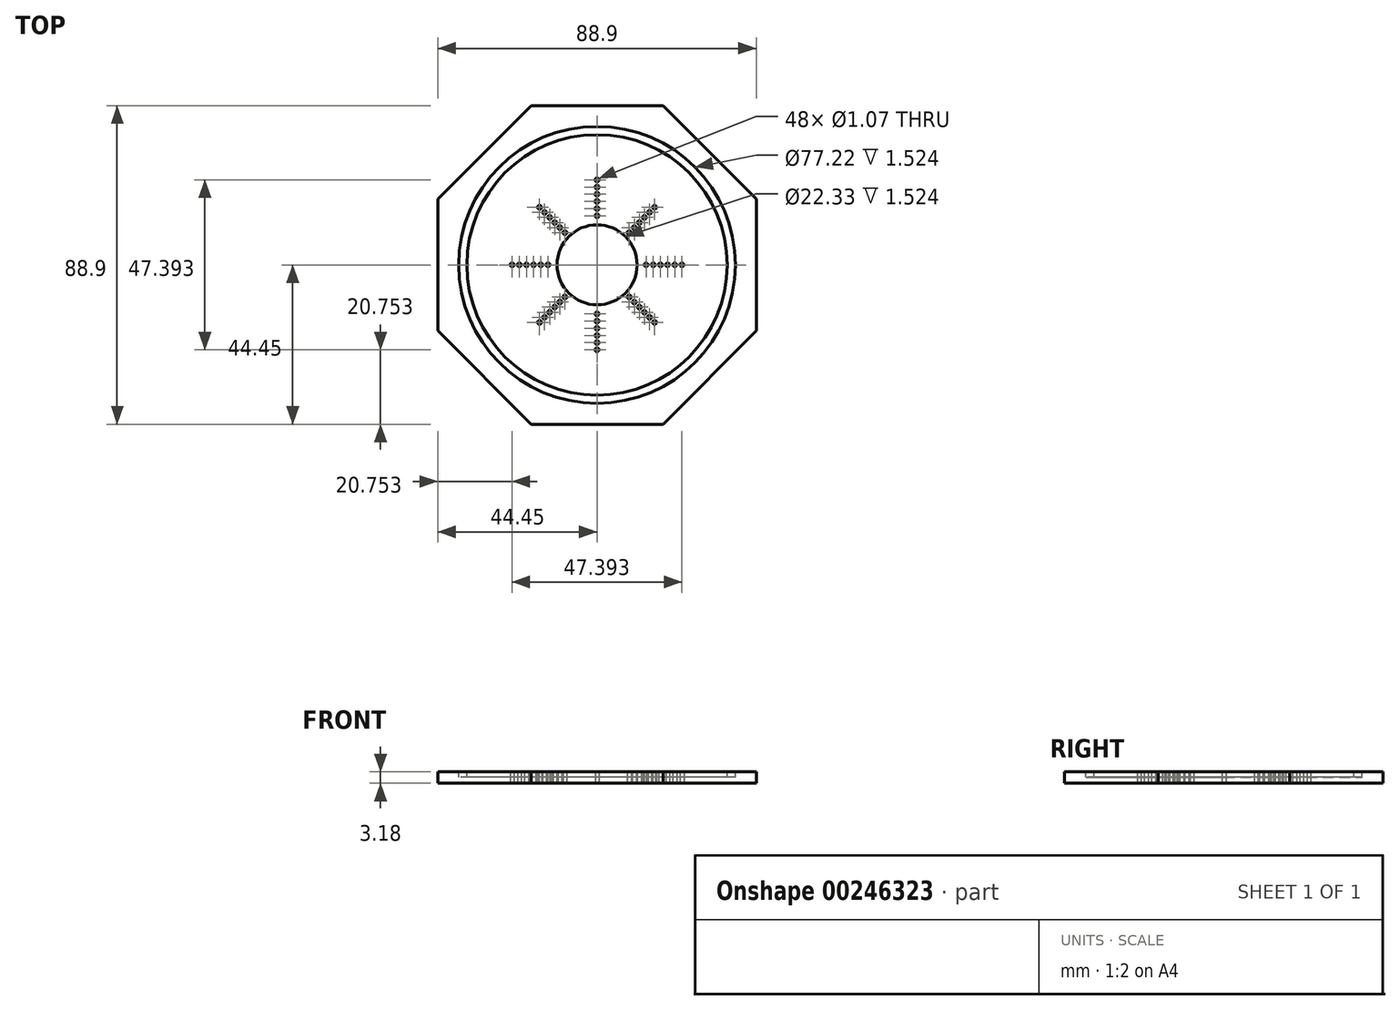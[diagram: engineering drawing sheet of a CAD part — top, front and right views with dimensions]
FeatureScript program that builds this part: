
annotation { "Feature Type Name" : "Feature", "Feature Type Description" : "" }
export const myFeature = defineFeature(function(context is Context, id is Id, definition is map)
    precondition{}
    {
        {
            var Q0;
            Q0=qCreatedBy(makeId("Top.planeOp"),FACE);
            var sketch = newSketch(context, id + "F0", { "sketchPlane" : qUnion([Q0])});
            skCircle(sketch, "E0", {"center": v(0, 0) * mm, "radius": 44.45 * mm, "construction": true});
            skLineSegment(sketch, "E1.bottom", {"start": v(-18.41, 44.45) * mm, "end": v(18.41, 44.45) * mm});
            skLineSegment(sketch, "E1.top", {"start": v(-18.41, -44.45) * mm, "end": v(18.41, -44.45) * mm});
            skLineSegment(sketch, "E1.left", {"start": v(-44.45, 18.41) * mm, "end": v(-44.45, -18.41) * mm});
            skLineSegment(sketch, "E1.right", {"start": v(44.45, 18.41) * mm, "end": v(44.45, -18.41) * mm});
            skLineSegment(sketch, "E2", {"start": v(-44.45, 18.41) * mm, "end": v(-18.41, 44.45) * mm});
            skLineSegment(sketch, "E3", {"start": v(0, 44.45) * mm, "end": v(0, -44.45) * mm, "construction": true});
            skLineSegment(sketch, "E4.MirrorCS", {"start": v(44.45, 18.41) * mm, "end": v(18.41, 44.45) * mm});
            skLineSegment(sketch, "E5", {"start": v(-44.45, 0) * mm, "end": v(44.45, 0) * mm});
            skLineSegment(sketch, "E6.MirrorCS", {"start": v(-44.45, -18.41) * mm, "end": v(-18.41, -44.45) * mm});
            skLineSegment(sketch, "E7.MirrorCS", {"start": v(44.45, -18.41) * mm, "end": v(18.41, -44.45) * mm});
            skPoint(sketch, "E8.orphan", {"position": v(-44.45, 44.45) * mm});
            skPoint(sketch, "E9.orphan", {"position": v(44.45, 44.45) * mm});
            skPoint(sketch, "E10.orphan", {"position": v(44.45, -44.45) * mm});
            skPoint(sketch, "E11.orphan", {"position": v(-44.45, -44.45) * mm});
            skSolve(sketch);
        }
        {
            var Q0;
            Q0=qSketchRegion(id+"F0",true);
            extrude(context, id + "F1", {"entities" : qUnion([Q0]), "depth" : 3.17 * mm});
        }
        {
            var Q0;
            Q0=makeQuery(id+"F1.opExtrude","CAP_FACE",FACE,{"disambiguationData":[OSD([sQuery(id+"F0.wireOp",EDGE,"E1.bottom"),sQuery(id+"F0.wireOp",EDGE,"E1.top"),sQuery(id+"F0.wireOp",EDGE,"E1.left"),sQuery(id+"F0.wireOp",EDGE,"E1.right")])],"isStart":false});
            var sketch = newSketch(context, id + "F2", { "sketchPlane" : qUnion([Q0])});
            skCircle(sketch, "E12", {"center": v(0, 0) * mm, "radius": 38.6 * mm});
            skCircle(sketch, "E13", {"center": v(0, 0) * mm, "radius": 36.32 * mm});
            skCircle(sketch, "E14", {"center": v(0, 0) * mm, "radius": 11.16 * mm});
            skSolve(sketch);
        }
        {
            var Q0;
            Q0=qSketchRegion(id+"F2",true);
            var Q1;
            Q1=makeQuery(id+"F2.imprint","IMPRINT",FACE,{"disambiguationData":[TD([[makeQuery(id+"F2.imprint","IMPRINT",EDGE,{"derivedFrom":sQuery(id+"F2.wireOp",EDGE,"E14")}),1.0]])]});
            extrude(context, id + "F3", {"entities" : qUnion([Q0, Q1]), "operationType" : NewBodyOperationType.REMOVE, "oppositeDirection" : true, "depth" : 1.52 * mm});
        }
        {
            var Q0;
            Q0=qCreatedBy(makeId("Top.planeOp"),FACE);
            var sketch = newSketch(context, id + "F4", { "sketchPlane" : qUnion([Q0])});
            skCircle(sketch, "E15", {"center": v(0, -13.7) * mm, "radius": 0.53 * mm});
            skCircle(sketch, "E16", {"center": v(0, -15.7) * mm, "radius": 0.53 * mm});
            skCircle(sketch, "E17", {"center": v(0, -17.7) * mm, "radius": 0.53 * mm});
            skCircle(sketch, "E18", {"center": v(0, -19.7) * mm, "radius": 0.53 * mm});
            skCircle(sketch, "E19", {"center": v(0, -21.7) * mm, "radius": 0.53 * mm});
            skCircle(sketch, "E20", {"center": v(0, -23.7) * mm, "radius": 0.53 * mm});
            skCircle(sketch, "E21.0", {"center": v(0, 0) * mm, "radius": 44.45 * mm, "construction": true});
            skLineSegment(sketch, "E22", {"start": v(31.43, 31.43) * mm, "end": v(-31.43, -31.43) * mm, "construction": true});
            skCircle(sketch, "E23", {"center": v(-8.98, -8.98) * mm, "radius": 0.53 * mm});
            skCircle(sketch, "E24", {"center": v(-10.4, -10.4) * mm, "radius": 0.53 * mm});
            skCircle(sketch, "E25", {"center": v(-11.8, -11.8) * mm, "radius": 0.53 * mm});
            skCircle(sketch, "E26", {"center": v(-13.22, -13.22) * mm, "radius": 0.53 * mm});
            skCircle(sketch, "E27", {"center": v(-14.63, -14.63) * mm, "radius": 0.53 * mm});
            skCircle(sketch, "E28", {"center": v(-16.05, -16.05) * mm, "radius": 0.53 * mm});
            skCircle(sketch, "E29.1.0", {"center": v(-21.7, 0) * mm, "radius": 0.53 * mm});
            skCircle(sketch, "E29.1.1", {"center": v(-23.7, 0) * mm, "radius": 0.53 * mm});
            skCircle(sketch, "E29.1.2", {"center": v(-13.7, 0) * mm, "radius": 0.53 * mm});
            skCircle(sketch, "E29.1.3", {"center": v(-17.7, 0) * mm, "radius": 0.53 * mm});
            skCircle(sketch, "E29.1.4", {"center": v(-15.7, 0) * mm, "radius": 0.53 * mm});
            skCircle(sketch, "E29.1.5", {"center": v(-19.7, 0) * mm, "radius": 0.53 * mm});
            skCircle(sketch, "E29.1.6", {"center": v(-16.05, 16.05) * mm, "radius": 0.53 * mm});
            skCircle(sketch, "E29.1.7", {"center": v(-14.63, 14.63) * mm, "radius": 0.53 * mm});
            skCircle(sketch, "E29.1.8", {"center": v(-8.98, 8.98) * mm, "radius": 0.53 * mm});
            skCircle(sketch, "E29.1.9", {"center": v(-10.4, 10.4) * mm, "radius": 0.53 * mm});
            skCircle(sketch, "E29.1.10", {"center": v(-13.22, 13.22) * mm, "radius": 0.53 * mm});
            skCircle(sketch, "E29.1.11", {"center": v(-11.8, 11.8) * mm, "radius": 0.53 * mm});
            skCircle(sketch, "E29.2.0", {"center": v(0, 21.7) * mm, "radius": 0.53 * mm});
            skCircle(sketch, "E29.2.1", {"center": v(0, 23.7) * mm, "radius": 0.53 * mm});
            skCircle(sketch, "E29.2.2", {"center": v(0, 13.7) * mm, "radius": 0.53 * mm});
            skCircle(sketch, "E29.2.3", {"center": v(0, 17.7) * mm, "radius": 0.53 * mm});
            skCircle(sketch, "E29.2.4", {"center": v(0, 15.7) * mm, "radius": 0.53 * mm});
            skCircle(sketch, "E29.2.5", {"center": v(0, 19.7) * mm, "radius": 0.53 * mm});
            skCircle(sketch, "E29.2.6", {"center": v(16.05, 16.05) * mm, "radius": 0.53 * mm});
            skCircle(sketch, "E29.2.7", {"center": v(14.63, 14.63) * mm, "radius": 0.53 * mm});
            skCircle(sketch, "E29.2.8", {"center": v(8.98, 8.98) * mm, "radius": 0.53 * mm});
            skCircle(sketch, "E29.2.9", {"center": v(10.4, 10.4) * mm, "radius": 0.53 * mm});
            skCircle(sketch, "E29.2.10", {"center": v(13.22, 13.22) * mm, "radius": 0.53 * mm});
            skCircle(sketch, "E29.2.11", {"center": v(11.8, 11.8) * mm, "radius": 0.53 * mm});
            skCircle(sketch, "E29.3.0", {"center": v(21.7, 0) * mm, "radius": 0.53 * mm});
            skCircle(sketch, "E29.3.1", {"center": v(23.7, 0) * mm, "radius": 0.53 * mm});
            skCircle(sketch, "E29.3.2", {"center": v(13.7, 0) * mm, "radius": 0.53 * mm});
            skCircle(sketch, "E29.3.3", {"center": v(17.7, 0) * mm, "radius": 0.53 * mm});
            skCircle(sketch, "E29.3.4", {"center": v(15.7, 0) * mm, "radius": 0.53 * mm});
            skCircle(sketch, "E29.3.5", {"center": v(19.7, 0) * mm, "radius": 0.53 * mm});
            skCircle(sketch, "E29.3.6", {"center": v(16.05, -16.05) * mm, "radius": 0.53 * mm});
            skCircle(sketch, "E29.3.7", {"center": v(14.63, -14.63) * mm, "radius": 0.53 * mm});
            skCircle(sketch, "E29.3.8", {"center": v(8.98, -8.98) * mm, "radius": 0.53 * mm});
            skCircle(sketch, "E29.3.9", {"center": v(10.4, -10.4) * mm, "radius": 0.53 * mm});
            skCircle(sketch, "E29.3.10", {"center": v(13.22, -13.22) * mm, "radius": 0.53 * mm});
            skCircle(sketch, "E29.3.11", {"center": v(11.8, -11.8) * mm, "radius": 0.53 * mm});
            skLineSegment(sketch, "E29.anchor1", {"start": v(0, 0) * mm, "end": v(-16.05, -16.05) * mm, "construction": true});
            skLineSegment(sketch, "E29.anchor2", {"start": v(0, 0) * mm, "end": v(16.05, -16.05) * mm, "construction": true});
            skSolve(sketch);
        }
        {
            var Q0;
            Q0 = qSketchRegion(id + "F4", true);
            extrude(context, id + "F5", {"entities" : qUnion([Q0]), "operationType" : NewBodyOperationType.REMOVE, "endBound" : BoundingType.THROUGH_ALL, "depth" : 25.4 * mm});
        }
    });
